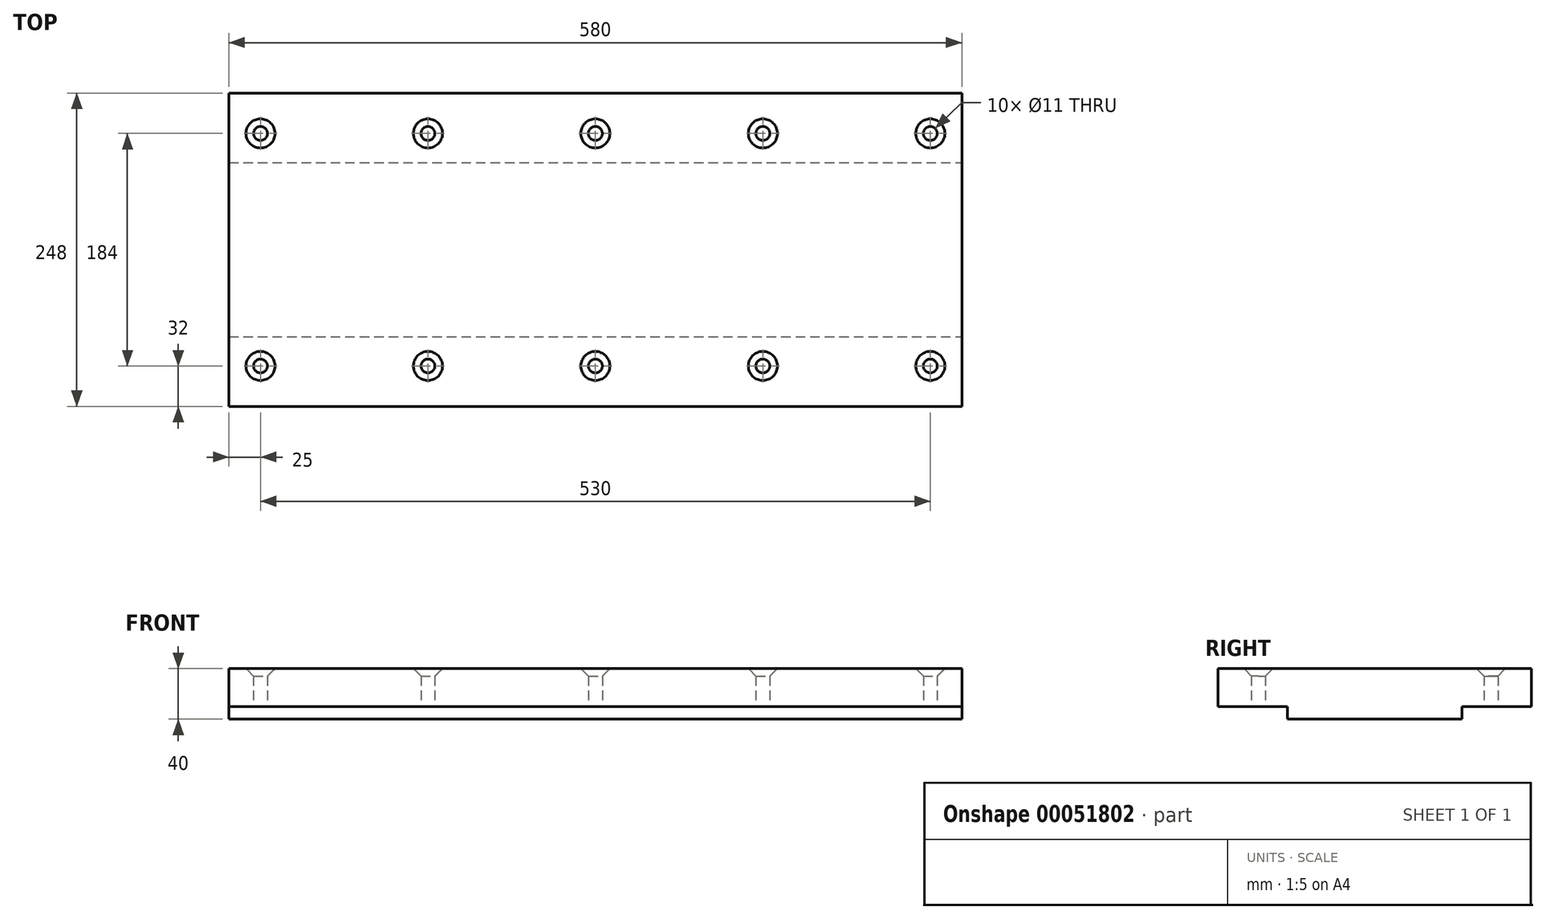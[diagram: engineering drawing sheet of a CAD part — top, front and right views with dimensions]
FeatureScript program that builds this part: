
annotation { "Feature Type Name" : "Feature", "Feature Type Description" : "" }
export const myFeature = defineFeature(function(context is Context, id is Id, definition is map)
    precondition{}
    {
        {
            var Q0;
            Q0=qCreatedBy(makeId("Top.planeOp"),FACE);
            var sketch = newSketch(context, id + "F0", { "sketchPlane" : qUnion([Q0])});
            skLineSegment(sketch, "E0.rect.bottom", {"start": v(290, 124) * mm, "end": v(-290, 124) * mm});
            skLineSegment(sketch, "E0.rect.top", {"start": v(290, -124) * mm, "end": v(-290, -124) * mm});
            skLineSegment(sketch, "E0.rect.left", {"start": v(290, 124) * mm, "end": v(290, -124) * mm});
            skLineSegment(sketch, "E0.rect.right", {"start": v(-290, 124) * mm, "end": v(-290, -124) * mm});
            skPoint(sketch, "E0.rect.middle", {"position": v(0, 0) * mm});
            skLineSegment(sketch, "E1", {"start": v(-290, 0) * mm, "end": v(290, 0) * mm, "construction": true});
            skLineSegment(sketch, "E2.rect.bottom", {"start": v(290, 92) * mm, "end": v(-290, 92) * mm, "construction": true});
            skLineSegment(sketch, "E2.rect.top", {"start": v(290, -92) * mm, "end": v(-290, -92) * mm, "construction": true});
            skLineSegment(sketch, "E2.rect.left", {"start": v(290, 92) * mm, "end": v(290, -92) * mm, "construction": true});
            skLineSegment(sketch, "E2.rect.right", {"start": v(-290, 92) * mm, "end": v(-290, -92) * mm, "construction": true});
            skLineSegment(sketch, "E3", {"start": v(-265, 124) * mm, "end": v(-265, -124) * mm, "construction": true});
            skLineSegment(sketch, "E4", {"start": v(-132.5, 124) * mm, "end": v(-132.5, -124) * mm, "construction": true});
            skLineSegment(sketch, "E5", {"start": v(0, 124) * mm, "end": v(0, -124) * mm, "construction": true});
            skLineSegment(sketch, "E6", {"start": v(132.5, 124) * mm, "end": v(132.5, -124) * mm, "construction": true});
            skLineSegment(sketch, "E7", {"start": v(265, 124) * mm, "end": v(265, -124) * mm, "construction": true});
            skCircle(sketch, "E8", {"center": v(265, -92) * mm, "radius": 5.5 * mm});
            skCircle(sketch, "E9", {"center": v(132.5, -92) * mm, "radius": 5.5 * mm});
            skCircle(sketch, "E10", {"center": v(-132.5, -92) * mm, "radius": 5.5 * mm});
            skCircle(sketch, "E11", {"center": v(-265, -92) * mm, "radius": 5.5 * mm});
            skCircle(sketch, "E12", {"center": v(0, -92) * mm, "radius": 5.5 * mm});
            skCircle(sketch, "E13", {"center": v(-265, 92) * mm, "radius": 5.5 * mm});
            skCircle(sketch, "E14", {"center": v(-132.5, 92) * mm, "radius": 5.5 * mm});
            skCircle(sketch, "E15", {"center": v(0, 92) * mm, "radius": 5.5 * mm});
            skCircle(sketch, "E16", {"center": v(132.5, 92) * mm, "radius": 5.5 * mm});
            skCircle(sketch, "E17", {"center": v(265, 92) * mm, "radius": 5.5 * mm});
            skSolve(sketch);
        }
        {
            var Q0;
            Q0 = qSketchRegion(id + "F0", true);
            extrude(context, id + "F1", {"entities" : qUnion([Q0]), "depth" : 40 * mm});
        }
        {
            var Q0;
            Q0=makeQuery(id+"F1.opExtrude","SWEPT_FACE",FACE,{"disambiguationData":[OSD([sQuery(id+"F0.wireOp",EDGE,"E0.rect.left")])]});
            var sketch = newSketch(context, id + "F2", { "sketchPlane" : qUnion([Q0])});
            skLineSegment(sketch, "E18", {"start": v(-124, 10) * mm, "end": v(124, 10) * mm, "construction": true});
            skLineSegment(sketch, "E19.rect.bottom", {"start": v(69, 0) * mm, "end": v(-69, 0) * mm});
            skLineSegment(sketch, "E19.rect.top", {"start": v(69, 0) * mm, "end": v(-69, 0) * mm});
            skLineSegment(sketch, "E19.rect.left", {"start": v(69, 0) * mm, "end": v(69, 0) * mm});
            skLineSegment(sketch, "E19.rect.right", {"start": v(-69, 0) * mm, "end": v(-69, 0) * mm});
            skPoint(sketch, "E19.rect.middle", {"position": v(0, 0) * mm});
            skLineSegment(sketch, "E20.bottom", {"start": v(-124, 10) * mm, "end": v(-69, 10) * mm});
            skLineSegment(sketch, "E20.top", {"start": v(-124, 0) * mm, "end": v(-69, 0) * mm});
            skLineSegment(sketch, "E20.left", {"start": v(-124, 10) * mm, "end": v(-124, 0) * mm});
            skLineSegment(sketch, "E20.right", {"start": v(-69, 10) * mm, "end": v(-69, 0) * mm});
            skLineSegment(sketch, "E21.bottom", {"start": v(124, 10) * mm, "end": v(69, 10) * mm});
            skLineSegment(sketch, "E21.top", {"start": v(124, 0) * mm, "end": v(69, 0) * mm});
            skLineSegment(sketch, "E21.left", {"start": v(124, 10) * mm, "end": v(124, 0) * mm});
            skLineSegment(sketch, "E21.right", {"start": v(69, 10) * mm, "end": v(69, 0) * mm});
            skSolve(sketch);
        }
        {
            var Q0;
            Q0=makeQuery(id+"F2.imprint","IMPRINT",FACE,{"disambiguationData":[TD([[makeQuery(id+"F2.imprint","IMPRINT",EDGE,{"derivedFrom":sQuery(id+"F2.wireOp",EDGE,"E21.bottom")}),1.0]])]});
            var Q1;
            Q1=makeQuery(id+"F2.imprint","IMPRINT",FACE,{"disambiguationData":[TD([[makeQuery(id+"F2.imprint","IMPRINT",EDGE,{"derivedFrom":sQuery(id+"F2.wireOp",EDGE,"E20.bottom")}),-1.0]])]});
            extrude(context, id + "F3", {"entities" : qUnion([Q0, Q1]), "operationType" : NewBodyOperationType.REMOVE, "endBound" : BoundingType.THROUGH_ALL, "oppositeDirection" : true, "depth" : 25 * mm});
        }
        {
            var Q0;
            Q0=makeQuery(id+"F1.opExtrude","CAP_EDGE",EDGE,{"disambiguationData":[OSD([sQuery(id+"F0.wireOp",EDGE,"E17")])],"isStart":false});
            var Q1;
            Q1=makeQuery(id+"F1.opExtrude","CAP_EDGE",EDGE,{"disambiguationData":[OSD([sQuery(id+"F0.wireOp",EDGE,"E16")])],"isStart":false});
            var Q2;
            Q2=makeQuery(id+"F1.opExtrude","CAP_EDGE",EDGE,{"disambiguationData":[OSD([sQuery(id+"F0.wireOp",EDGE,"E8")])],"isStart":false});
            var Q3;
            Q3=makeQuery(id+"F1.opExtrude","CAP_EDGE",EDGE,{"disambiguationData":[OSD([sQuery(id+"F0.wireOp",EDGE,"E9")])],"isStart":false});
            var Q4;
            Q4=makeQuery(id+"F1.opExtrude","CAP_EDGE",EDGE,{"disambiguationData":[OSD([sQuery(id+"F0.wireOp",EDGE,"E12")])],"isStart":false});
            var Q5;
            Q5=makeQuery(id+"F1.opExtrude","CAP_EDGE",EDGE,{"disambiguationData":[OSD([sQuery(id+"F0.wireOp",EDGE,"E15")])],"isStart":false});
            var Q6;
            Q6=makeQuery(id+"F1.opExtrude","CAP_EDGE",EDGE,{"disambiguationData":[OSD([sQuery(id+"F0.wireOp",EDGE,"E10")])],"isStart":false});
            var Q7;
            Q7=makeQuery(id+"F1.opExtrude","CAP_EDGE",EDGE,{"disambiguationData":[OSD([sQuery(id+"F0.wireOp",EDGE,"E14")])],"isStart":false});
            var Q8;
            Q8=makeQuery(id+"F1.opExtrude","CAP_EDGE",EDGE,{"disambiguationData":[OSD([sQuery(id+"F0.wireOp",EDGE,"E13")])],"isStart":false});
            var Q9;
            Q9=makeQuery(id+"F1.opExtrude","CAP_EDGE",EDGE,{"disambiguationData":[OSD([sQuery(id+"F0.wireOp",EDGE,"E11")])],"isStart":false});
            chamfer(context, id + "F4", {"entities" : qUnion([Q0, Q1, Q2, Q3, Q4, Q5, Q6, Q7, Q8, Q9]), "chamferType" : ChamferType.OFFSET_ANGLE, "width" : 6 * mm, "oppositeDirection" : false, "angle" : 45 * degree, "tangentPropagation" : true});
        }
    });
